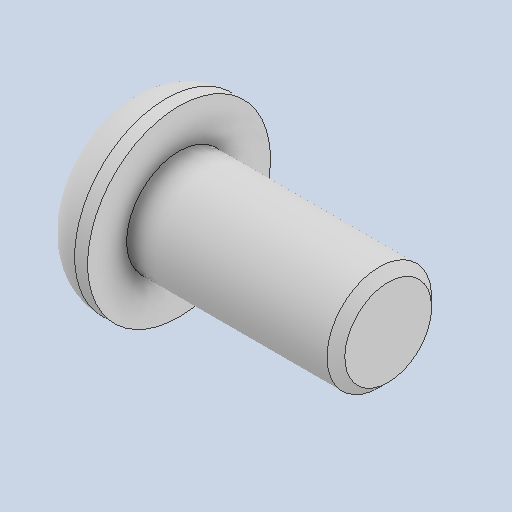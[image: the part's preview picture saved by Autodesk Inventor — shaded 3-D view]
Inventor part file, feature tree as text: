
AUTODESK INVENTOR PART (.ipt)
format: ipt  version: 2022 (Build 260153000, 153)  size: 135,680 bytes
history: native  units: in
note: dims shown in document units (in); Inventor stores cm internally (conversion verified against a paired STEP export)
features: chamfer x1
ambient origin geometry x8: Origin, YZ Plane, XZ Plane, XY Plane, X Axis, Y Axis, Z Axis, Center Point
bodies: Solid1 (feature_tree)
feature tree (1):
  chamfer  "Chamfer1"  [1 undecoded]
note: 1 required parameter value undecoded (feature->parameter linkage not recoverable at this tier; creation-order binding heuristic only, values carry confidence <= 0.55)
